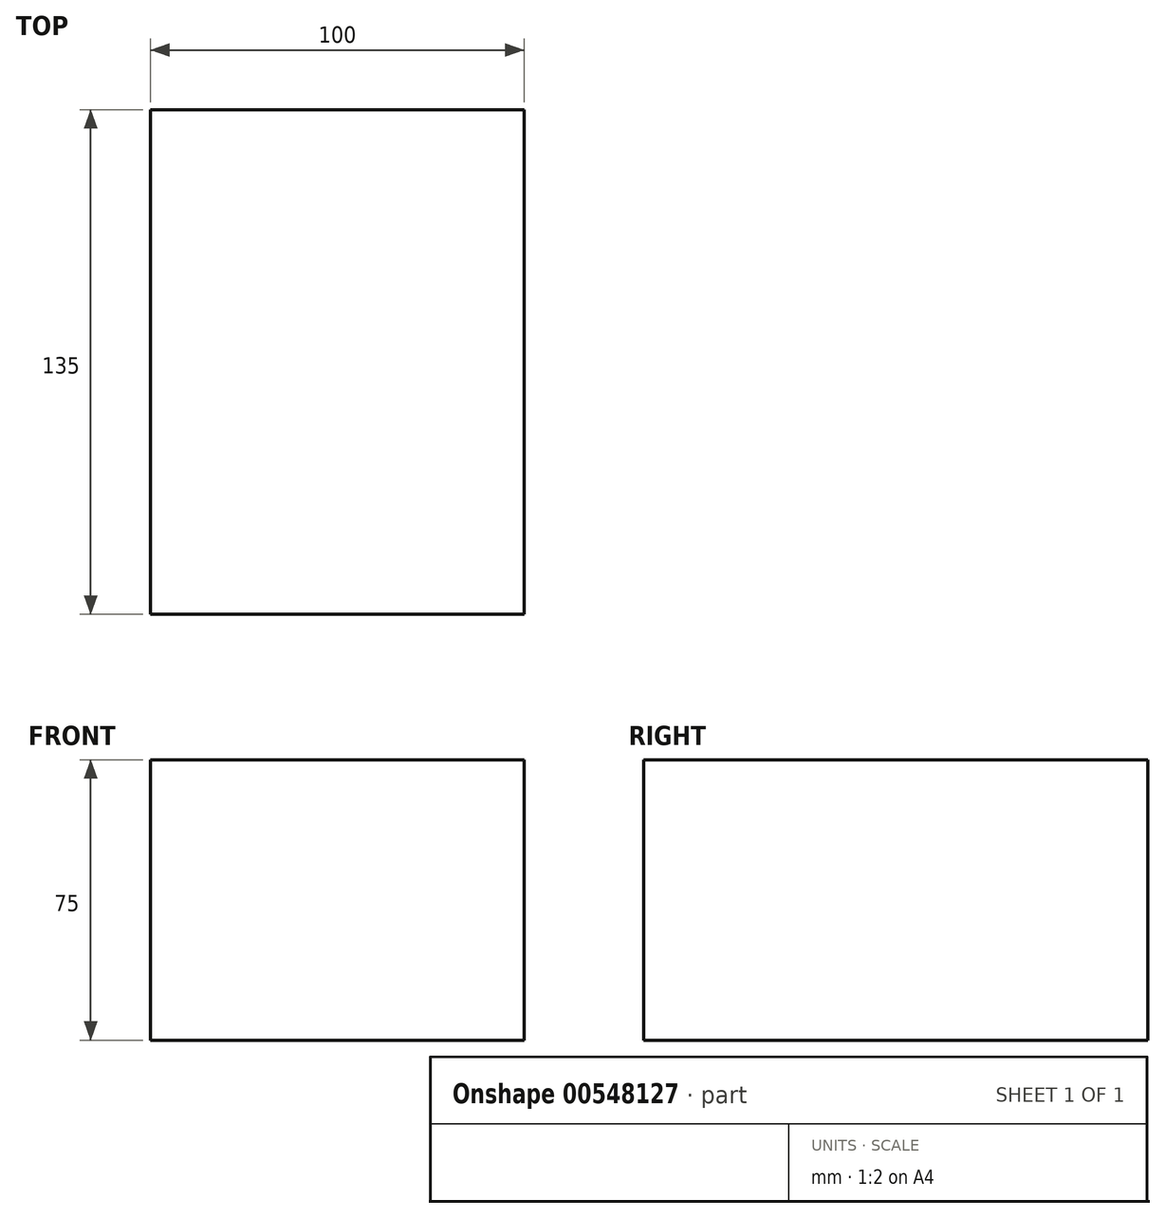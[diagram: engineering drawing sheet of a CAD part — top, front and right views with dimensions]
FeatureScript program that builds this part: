
annotation { "Feature Type Name" : "Feature", "Feature Type Description" : "" }
export const myFeature = defineFeature(function(context is Context, id is Id, definition is map)
    precondition{}
    {
        {
            var Q0;
            Q0=qCreatedBy(makeId("Top.planeOp"),FACE);
            var sketch = newSketch(context, id + "F0", { "sketchPlane" : qUnion([Q0])});
            skLineSegment(sketch, "E0.bottom", {"start": v(-71.54, 80.48) * mm, "end": v(28.46, 80.48) * mm});
            skLineSegment(sketch, "E0.top", {"start": v(-71.54, -54.52) * mm, "end": v(28.46, -54.52) * mm});
            skLineSegment(sketch, "E0.left", {"start": v(-71.54, 80.48) * mm, "end": v(-71.54, -54.52) * mm});
            skLineSegment(sketch, "E0.right", {"start": v(28.46, 80.48) * mm, "end": v(28.46, -54.52) * mm});
            skSolve(sketch);
        }
        {
            var Q0;
            Q0=makeQuery(id+"F0.imprint","IMPRINT",FACE,{"disambiguationData":[TD([[makeQuery(id+"F0.imprint","IMPRINT",EDGE,{"derivedFrom":sQuery(id+"F0.wireOp",EDGE,"E0.bottom")}),-1.0]])]});
            extrude(context, id + "F1", {"entities" : qUnion([Q0]), "depth" : 75 * mm, "offsetDistance" : 25 * mm});
        }
    });
